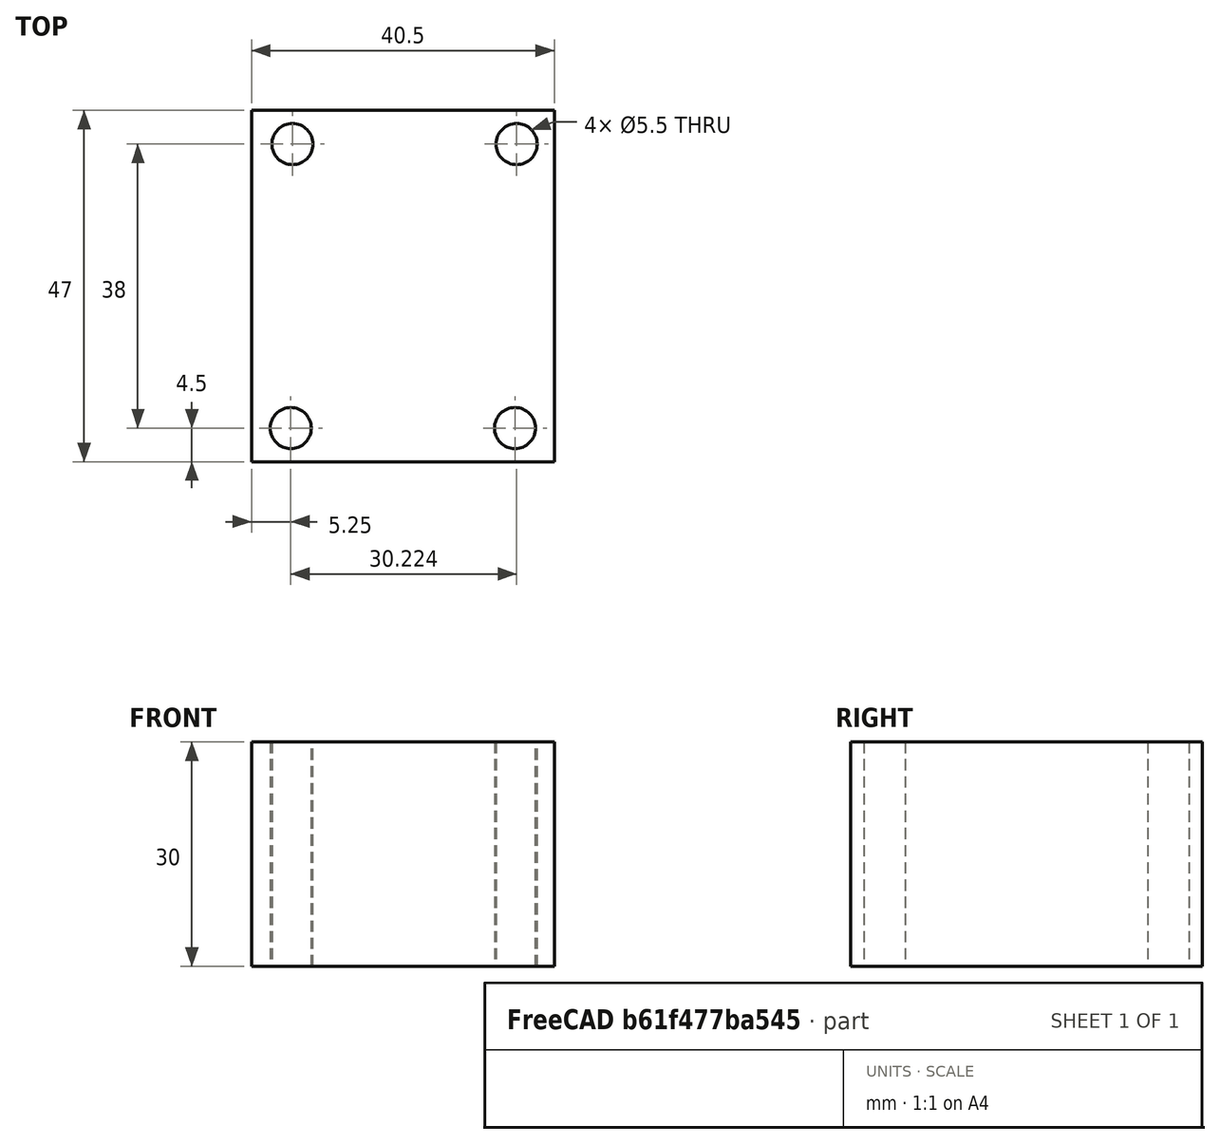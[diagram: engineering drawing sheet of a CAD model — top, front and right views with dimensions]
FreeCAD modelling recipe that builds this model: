
FCSTD DOCUMENT  (FreeCAD 0.16R6348 (Git))
Label: TopeHerramienta
License: All rights reserved
LicenseURL: http://es.wikipedia.org/wiki/Todos_los_derechos_reservados
objects: Sketcher::SketchObject×1, PartDesign::Pad×1, Part::Feature×1
note: 4 computed .brp shape members not serialized (recipe doc carries the construction recipe); baked Part::Feature solids carry a one-line shape summary decoded from their .brp

FEATURE [Sketcher::SketchObject] Sketch
  sketch-geometry (8):
    g0: LineSegment StartX=0 StartY=0 StartZ=0 EndX=40.5 EndY=0 EndZ=0
    g1: LineSegment StartX=40.5 StartY=0 StartZ=0 EndX=40.5 EndY=47 EndZ=0
    g2: LineSegment StartX=40.5 StartY=47 StartZ=0 EndX=0 EndY=47 EndZ=0
    g3: LineSegment StartX=0 StartY=47 StartZ=0 EndX=0 EndY=0 EndZ=0
    g4: Circle CenterX=5.25 CenterY=4.5 CenterZ=0 NormalX=0 NormalY=0 NormalZ=1 Radius=2.75
    g5: Circle CenterX=35.25 CenterY=4.5 CenterZ=0 NormalX=0 NormalY=0 NormalZ=1 Radius=2.75
    g6: Circle CenterX=35.4736 CenterY=42.5 CenterZ=0 NormalX=0 NormalY=0 NormalZ=1 Radius=2.75
    g7: Circle CenterX=5.47365 CenterY=42.5 CenterZ=0 NormalX=0 NormalY=0 NormalZ=1 Radius=2.75
  constraints (22):
    c: Coincident(g0,g1)
    c: Coincident(g1,g2)
    c: Coincident(g2,g3)
    c: Coincident(g3,g0)
    c: Horizontal(g0)
    c: Horizontal(g2)
    c: Vertical(g1)
    c: Vertical(g3)
    c: Coincident(g0,g-1)
    c: DistanceX(g2,g1) = 40.5
    c: DistanceY(g-1,g2) = 47
    c: Radius(g7) = 2.75
    c: Radius(g6) = 2.75
    c: Radius(g4) = 2.75
    c: Radius(g5) = 2.75
    c: DistanceX(g4,g5) = 30
    c: DistanceY(g4,g7) = 38
    c: DistanceX(g7,g6) = 30
    c: DistanceY(g6,g5) = -38
    c: DistanceY(g-1,g4) = 4.5
    c: DistanceX(g-1,g4) = 5.25
    c: DistanceY(g-1,g5) = 4.5
FEATURE [PartDesign::Pad] Pad
  Length = 30
  Length2 = 100
  Sketch = -> Sketch
  Type = 0
FEATURE [Part::Feature] Pad001
  shape: bbox 40.5 x 47 x 30 mm, 10 faces (baked)
